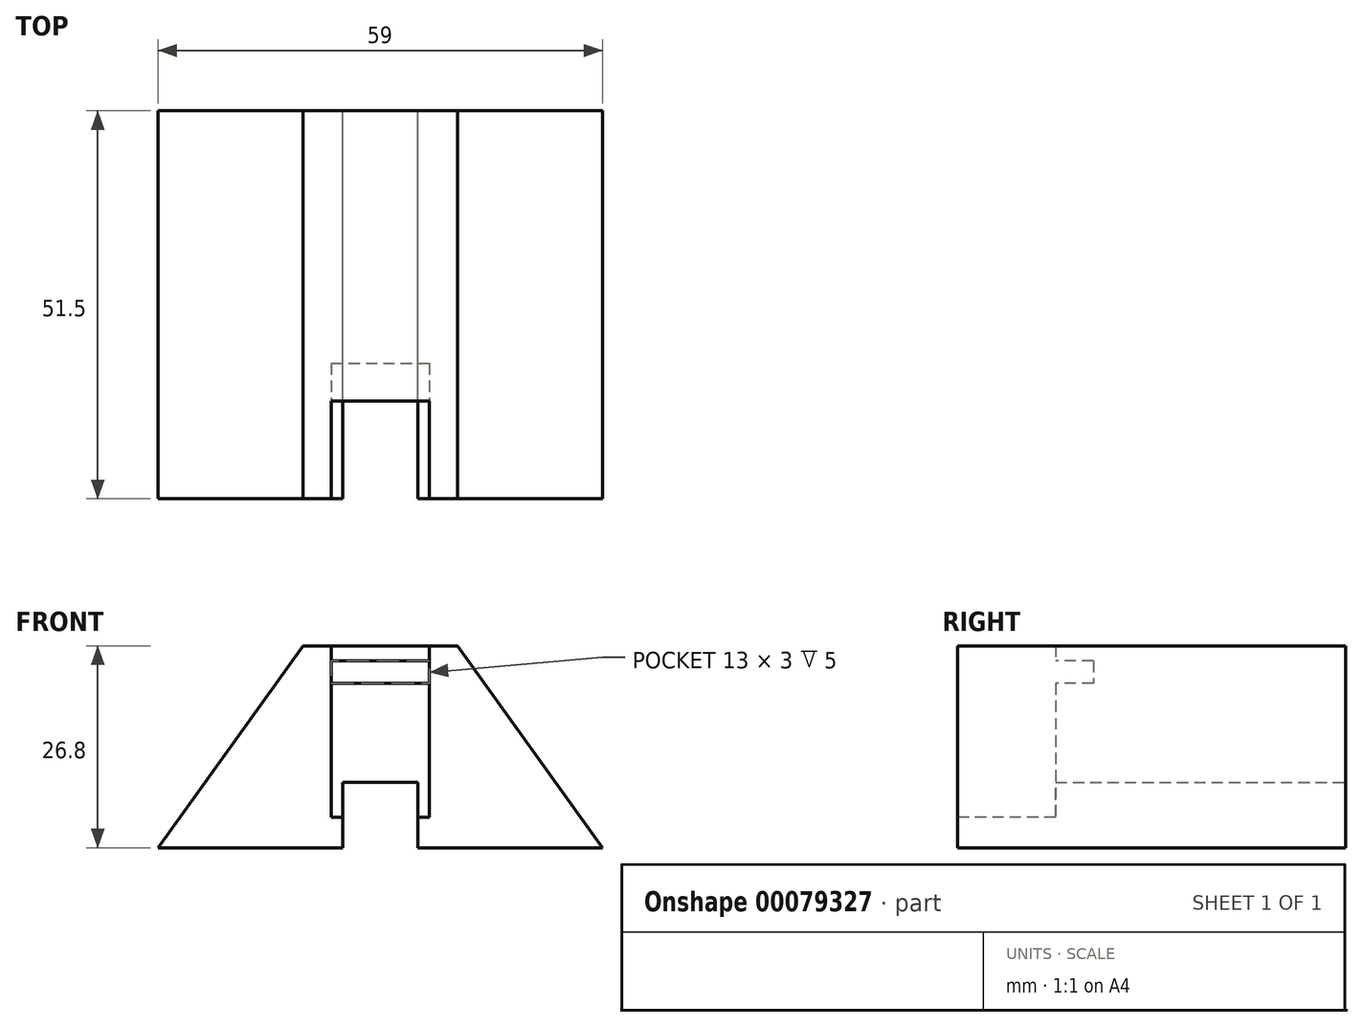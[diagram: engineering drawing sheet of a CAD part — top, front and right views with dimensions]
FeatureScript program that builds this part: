
annotation { "Feature Type Name" : "Feature", "Feature Type Description" : "" }
export const myFeature = defineFeature(function(context is Context, id is Id, definition is map)
    precondition{}
    {
        {
            var Q0;
            Q0=qCreatedBy(makeId("Front.planeOp"),FACE);
            var sketch = newSketch(context, id + "F0", { "sketchPlane" : qUnion([Q0])});
            skLineSegment(sketch, "E0", {"start": v(-29.5, 0) * mm, "end": v(-5, 0) * mm});
            skLineSegment(sketch, "E1", {"start": v(29.5, 0) * mm, "end": v(10.25, 26.8) * mm});
            skLineSegment(sketch, "E2", {"start": v(10.25, 26.8) * mm, "end": v(-10.25, 26.8) * mm});
            skLineSegment(sketch, "E3", {"start": v(-10.25, 26.8) * mm, "end": v(-29.5, 0) * mm});
            skLineSegment(sketch, "E4.top", {"start": v(-5, 8.67) * mm, "end": v(5, 8.67) * mm});
            skLineSegment(sketch, "E4.left", {"start": v(-5, 0) * mm, "end": v(-5, 8.67) * mm});
            skLineSegment(sketch, "E4.right", {"start": v(5, 0) * mm, "end": v(5, 8.67) * mm});
            skLineSegment(sketch, "E5.trimOffspring", {"start": v(5, 0) * mm, "end": v(29.5, 0) * mm});
            skSolve(sketch);
        }
        {
            var Q0;
            Q0 = qSketchRegion(id + "F0", true);
            extrude(context, id + "F1", {"entities" : qUnion([Q0]), "depth" : 51.5 * mm});
        }
        {
            var Q0;
            Q0=makeQuery(id+"F1.opExtrude","CAP_FACE",FACE,{"disambiguationData":[OSD([sQuery(id+"F0.wireOp",EDGE,"E0"),sQuery(id+"F0.wireOp",EDGE,"E1"),sQuery(id+"F0.wireOp",EDGE,"E2"),sQuery(id+"F0.wireOp",EDGE,"E3"),sQuery(id+"F0.wireOp",EDGE,"E4.top"),sQuery(id+"F0.wireOp",EDGE,"E4.left"),sQuery(id+"F0.wireOp",EDGE,"E4.right"),sQuery(id+"F0.wireOp",EDGE,"E5.trimOffspring")])],"isStart":false});
            var sketch = newSketch(context, id + "F2", { "sketchPlane" : qUnion([Q0])});
            skLineSegment(sketch, "E6.bottom", {"start": v(-6.5, 26.8) * mm, "end": v(6.5, 26.8) * mm});
            skLineSegment(sketch, "E6.top", {"start": v(-6.5, 4.05) * mm, "end": v(6.5, 4.05) * mm});
            skLineSegment(sketch, "E6.left", {"start": v(-6.5, 26.8) * mm, "end": v(-6.5, 4.05) * mm});
            skLineSegment(sketch, "E6.right", {"start": v(6.5, 26.8) * mm, "end": v(6.5, 4.05) * mm});
            skSolve(sketch);
        }
        {
            var Q0;
            Q0 = qSketchRegion(id + "F2", true);
            extrude(context, id + "F3", {"entities" : qUnion([Q0]), "operationType" : NewBodyOperationType.REMOVE, "oppositeDirection" : true, "depth" : 13 * mm});
        }
        {
            var Q0;
            Q0=makeQuery(id+"F3.boolean.opBoolean","COPY",FACE,{"derivedFrom":makeQuery(id+"F3.opExtrude","CAP_FACE",FACE,{"disambiguationData":[OSD([sQuery(id+"F2.wireOp",EDGE,"E6.bottom"),sQuery(id+"F2.wireOp",EDGE,"E6.top"),sQuery(id+"F2.wireOp",EDGE,"E6.left"),sQuery(id+"F2.wireOp",EDGE,"E6.right")])],"isStart":false})});
            var sketch = newSketch(context, id + "F4", { "sketchPlane" : qUnion([Q0])});
            skLineSegment(sketch, "E7.bottom", {"start": v(-6.5, 24.8) * mm, "end": v(6.5, 24.8) * mm});
            skLineSegment(sketch, "E7.top", {"start": v(-6.5, 21.8) * mm, "end": v(6.5, 21.8) * mm});
            skLineSegment(sketch, "E7.left", {"start": v(-6.5, 24.8) * mm, "end": v(-6.5, 21.8) * mm});
            skLineSegment(sketch, "E7.right", {"start": v(6.5, 24.8) * mm, "end": v(6.5, 21.8) * mm});
            skSolve(sketch);
        }
        {
            var Q0;
            Q0 = qSketchRegion(id + "F4", true);
            extrude(context, id + "F5", {"entities" : qUnion([Q0]), "operationType" : NewBodyOperationType.REMOVE, "oppositeDirection" : true, "depth" : 5 * mm});
        }
    });
